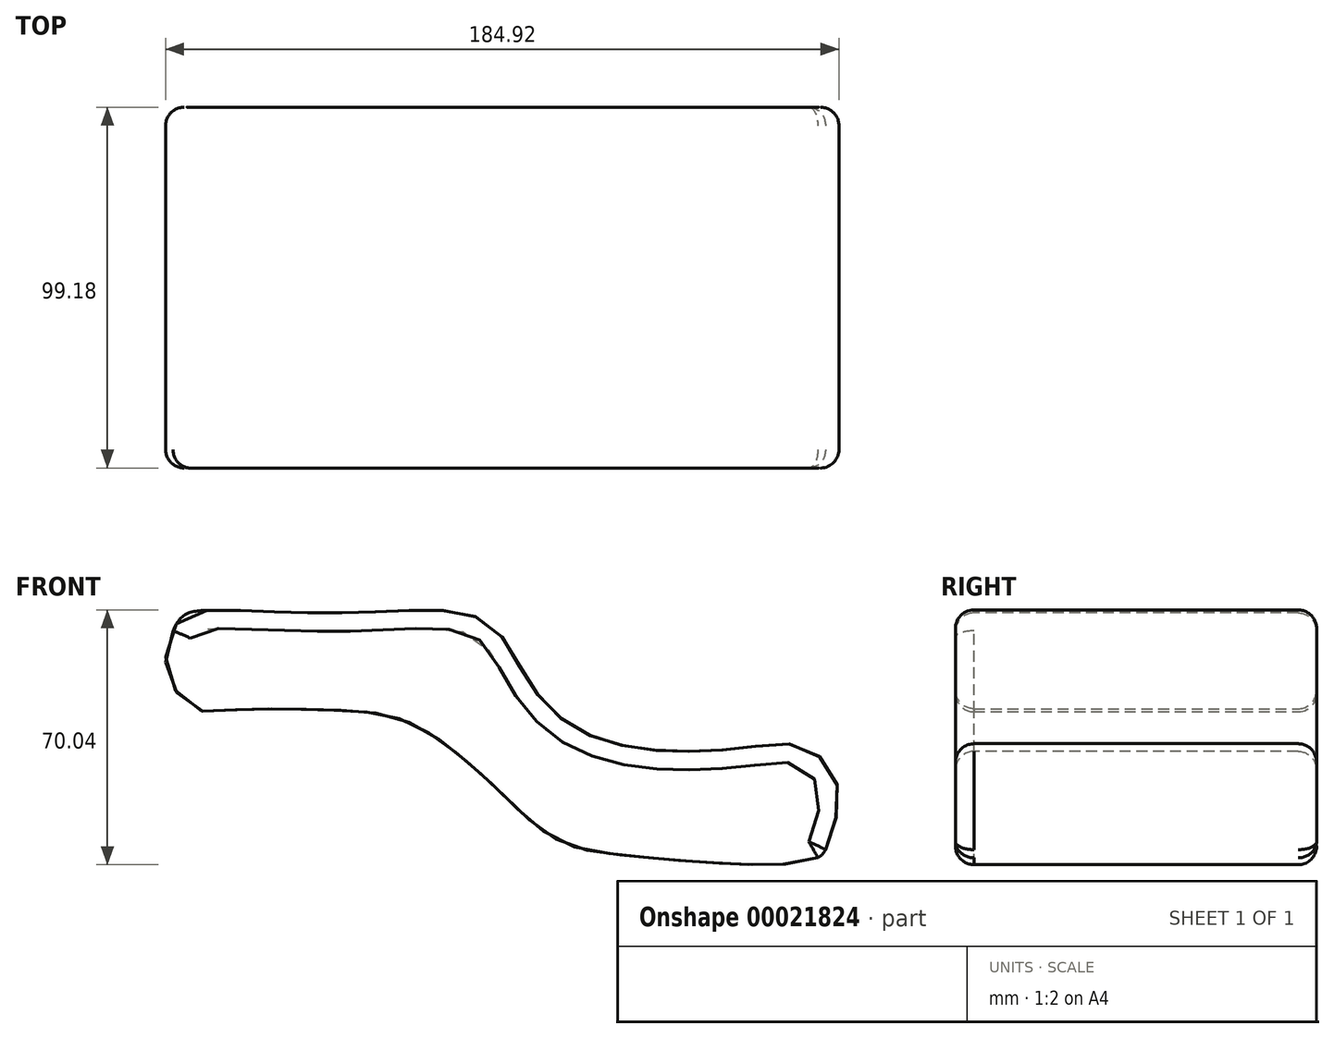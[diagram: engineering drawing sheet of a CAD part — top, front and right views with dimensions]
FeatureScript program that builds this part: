
annotation { "Feature Type Name" : "Feature", "Feature Type Description" : "" }
export const myFeature = defineFeature(function(context is Context, id is Id, definition is map)
    precondition{}
    {
        {
            var Q0;
            Q0=qCreatedBy(makeId("Front.planeOp"),FACE);
            var sketch = newSketch(context, id + "F0", { "sketchPlane" : qUnion([Q0])});
            skFitSpline(sketch, "E0", {"points": [v(-89.11, 37.76) * mm, v(-51.46, 37.13) * mm, v(-19.45, 37.44) * mm, v(-8.16, 31.8) * mm, v(0, 18.62) * mm, v(10.67, 7) * mm, v(29.5, 0) * mm, v(59.62, 0) * mm, v(76.56, 0) * mm, v(85.35, -11.82) * mm, v(82.83, -25) * mm, v(78.76, -30.64) * mm, v(28.87, -29.7) * mm, v(7.53, -25) * mm, v(-7.53, -12.13) * mm, v(-21.34, 0) * mm, v(-35.77, 8.26) * mm, v(-56.48, 10.46) * mm, v(-80.32, 10.46) * mm, v(-92.25, 11.09) * mm, v(-99.15, 21.44) * mm, v(-98.52, 28.97) * mm, v(-95.39, 35.56) * mm, v(-89.11, 37.76) * mm]});
            skSolve(sketch);
        }
        {
            var Q0;
            Q0 = qSketchRegion(id + "F0", true);
            extrude(context, id + "F1", {"entities" : qUnion([Q0]), "depth" : 99.18 * mm});
        }
        {
            var Q0;
            Q0=makeQuery(id+"F1.opExtrude","CAP_FACE",FACE,{"disambiguationData":[OSD([sQuery(id+"F0.wireOp",EDGE,"E0")])],"isStart":false});
            var Q1;
            Q1=makeQuery(id+"F1.opExtrude","CAP_FACE",FACE,{"disambiguationData":[OSD([sQuery(id+"F0.wireOp",EDGE,"E0")])],"isStart":true});
            fillet(context, id + "F2", {"entities" : qUnion([Q0, Q1]), "radius" : 5.08 * mm, "tangentPropagation" : true, "allowEdgeOverflow" : false});
        }
    });
